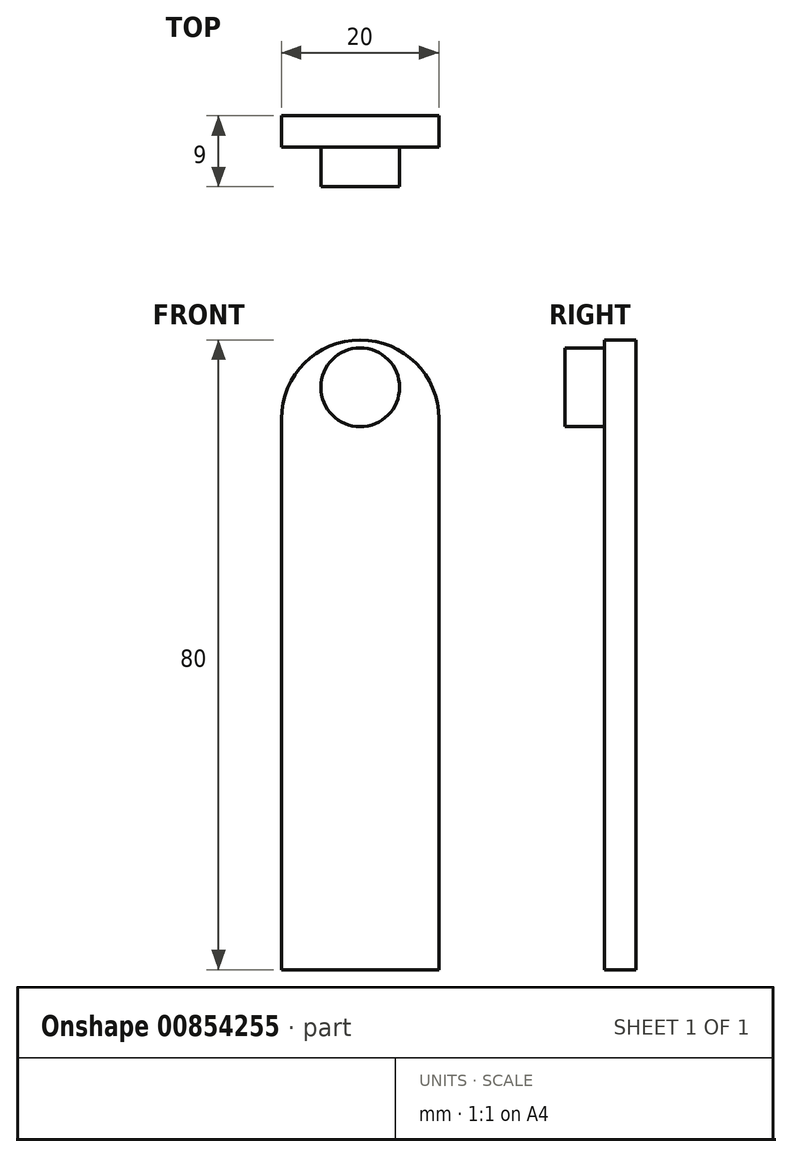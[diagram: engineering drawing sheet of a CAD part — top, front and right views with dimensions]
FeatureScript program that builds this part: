
annotation { "Feature Type Name" : "Feature", "Feature Type Description" : "" }
export const myFeature = defineFeature(function(context is Context, id is Id, definition is map)
    precondition{}
    {
        {
            var Q0;
            Q0=qCreatedBy(makeId("Top.planeOp"),FACE);
            var sketch = newSketch(context, id + "F0", { "sketchPlane" : qUnion([Q0])});
            skLineSegment(sketch, "E0.bottom", {"start": v(-10, 2) * mm, "end": v(10, 2) * mm});
            skLineSegment(sketch, "E0.top", {"start": v(-10, -2) * mm, "end": v(10, -2) * mm});
            skLineSegment(sketch, "E0.left", {"start": v(-10, 2) * mm, "end": v(-10, -2) * mm});
            skLineSegment(sketch, "E0.right", {"start": v(10, 2) * mm, "end": v(10, -2) * mm});
            skSolve(sketch);
        }
        {
            var Q0;
            Q0 = qSketchRegion(id + "F0", true);
            extrude(context, id + "F1", {"entities" : qUnion([Q0]), "depth" : 70 * mm, "offsetDistance" : 25 * mm});
        }
        {
            var Q0;
            Q0=qCreatedBy(makeId("Front.planeOp"),FACE);
            var sketch = newSketch(context, id + "F2", { "sketchPlane" : qUnion([Q0])});
            skArc(sketch, "E1", {"start": v(10, 70) * mm, "mid": v(0, 80) * mm, "end": v(-10, 70) * mm});
            skLineSegment(sketch, "E2", {"start": v(-10, 70) * mm, "end": v(10, 70) * mm});
            skSolve(sketch);
        }
        {
            var Q0;
            Q0 = qSketchRegion(id + "F2", true);
            extrude(context, id + "F3", {"entities" : qUnion([Q0]), "operationType" : NewBodyOperationType.ADD, "endBound" : BoundingType.SYMMETRIC, "depth" : 4 * mm, "offsetDistance" : 25 * mm});
        }
        {
            var Q0;
            Q0=qCreatedBy(makeId("Front.planeOp"),FACE);
            var sketch = newSketch(context, id + "F4", { "sketchPlane" : qUnion([Q0])});
            skCircle(sketch, "E3", {"center": v(0, 74) * mm, "radius": 5 * mm});
            skSolve(sketch);
        }
        {
            var Q0;
            Q0 = qSketchRegion(id + "F4", true);
            extrude(context, id + "F5", {"entities" : qUnion([Q0]), "operationType" : NewBodyOperationType.REMOVE, "depth" : 25 * mm, "offsetDistance" : 25 * mm});
        }
        {
            var Q0;
            Q0=makeQuery(id+"F5.boolean.opBoolean","COPY",FACE,{"derivedFrom":makeQuery(id+"F5.opExtrude","CAP_FACE",FACE,{"disambiguationData":[OSD([sQuery(id+"F4.wireOp",EDGE,"E3")])],"isStart":true})});
            var sketch = newSketch(context, id + "F6", { "sketchPlane" : qUnion([Q0])});
            skCircle(sketch, "E4", {"center": v(0, 74) * mm, "radius": 5 * mm});
            skSolve(sketch);
        }
        {
            var Q0;
            Q0 = qSketchRegion(id + "F6", true);
            extrude(context, id + "F7", {"entities" : qUnion([Q0]), "operationType" : NewBodyOperationType.ADD, "depth" : 7 * mm, "offsetDistance" : 25 * mm});
        }
    });
